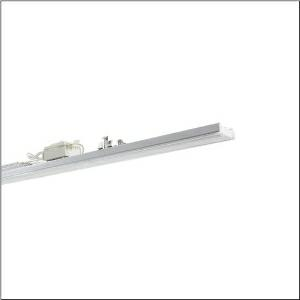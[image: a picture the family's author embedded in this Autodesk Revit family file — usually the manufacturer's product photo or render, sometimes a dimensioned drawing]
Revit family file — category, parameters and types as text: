
# Revit family: licross_r__21_recessed_ho_52tl18dv4l2m_8c23
name_source: partatom
category: Lighting Fixtures
units: mm (PartAtom-declared; Revit-internal decimal feet)

## family parameters
Cut with Voids When Loaded = No
Host = Face
Light Source = No
Part Type = Normal
Room Calculation Point = No
Round Connector Dimension = Use Diameter
Shared = No

## types (1)
- --- (1 x LED, 22480 lm, 125.6 W, 4000K)
    Apparent Load = 126 VA
    CIE Flux Codes = 75 94 99 100 100
    Color Rendering = 80
    Color Temperature = 4000K
    Default Elevation = 1800 mm
    Description = Licross® 21 Recessed HO, luminaire insert, of sheet steel, galvanised, coil coated, white, length: 2.250mm, width: 66mm, height: 67mm, LED rated luminous flux: 22.480lm, light colour: 840, control gear: DALI 2, with plug, 5-pole, with phase selection, mains connection: 220..240V, AC, 50/60Hz, rated input power: 126W, halogen-free wiring, primary light control with lens, of plastic, primary optical cover: cover, of PMMA, light emission: direct distribution, primary light characteristic: symmetric, protection rating (complete): IP40, insulation class (complete): insulation class I (protective earthing), certification: CE, ENEC, VDE, UKCA, protection symbol: D if used in an environment without relevant dust loads with corresponding accessories, impact resistance: IK06, permissible ambient temperature for indoor applications: -40..+30°C, corresponds to IFS (International Featured Standards) requirements for safety and quality in the food industry, reducing of maximum allowable ambient temperature of 5°C with ceiling mounting, LABS conformity tested according to VDMA 24364:2018-05, packaging unit: 1 piece
    Height = 58 mm
    Lamp = 1 x LED
    Lamp Light Flux = 22480 lm
    Lamp Power = 125.6 W
    Lamp count = 1
    Length = 2250 mm
    Luminous efficacy = 179 lm/W
    Manufacturer = Siteco
    ModVariant = No
    Model = 52TL18DV4L2M
    Mounting Place = Ceiling
    Mounting Type = Pendant
    Number of Poles = 1
    OnlyDefault = Yes
    Power Factor = 1
    Product Name = Licross® 21 Recessed HO
    Product group = luminaire insert
    ProductGroupID = 902
    Protection Class = Protection class I
    Protection Degree = IP 40
    RLX_Detail_Level = 1
    RLX_Emergency_Light_Flux = 0 lm
    RLX_Emergency_Type = 0
    RLX_Emergency_Type_DB = No
    RlxData = <blob elided: 29529 chars, md5=6f359991>
    Socket = socket
    Standby Power = 0 W
    System Light Flux = 22480 lm
    System Power = 126 W
    Type Comments = factory setting: luminous flux: 100 % | dim-lin: 254 | 489 mA
    Type Image = l_1296930.jpg
    URL = http://relux.com
    VarID = @adj_125836
    Voltage = 0 V
    Weight = 0.00 kg
    Width = 66 mm

## geometry (parser evidence)
native form markers: Blend x4, Sweep x8
no freeform markers — native parametric forms only
